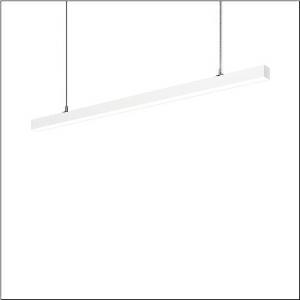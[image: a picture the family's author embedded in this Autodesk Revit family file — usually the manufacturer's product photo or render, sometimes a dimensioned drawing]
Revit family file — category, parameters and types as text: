
# Revit family: silica_r__21_51mx30db45wb_134d
name_source: partatom
category: Lighting Fixtures
units: mm (PartAtom-declared; Revit-internal decimal feet)

## family parameters
Cut with Voids When Loaded = No
Host = Face
Light Source = No
Part Type = Normal
Room Calculation Point = No
Round Connector Dimension = Use Diameter
Shared = No

## types (1)
- --- (1 x LED, 5260 lm, 32 W, 4000K)
    Apparent Load = 32 VA
    CIE Flux Codes = 47 79 96 57 100
    Color Rendering = 80
    Color Temperature = 4000K
    Default Elevation = 1800 mm
    Description = Silica® 21, office luminaire, primary optical cover: cover, of PMMA, opal, light emission: direct/indirect distribution, primary light characteristic: symmetric, installation type: suspended mounting, LED, rated luminous flux: 5.260lm, luminous efficacy: 164lm/W, light colour: 840, colour temperature: 4000K, control gear: DALI 2, with terminal, 3+2-pole, max. 2.5mm², mains connection: 220..240V, AC, 50/60Hz, rated input power: 32W, luminaire housing, of aluminium, traffic white (RAL 9016), length: 1.504mm, width: 53mm, height: 53mm, protection rating (complete): IP20, insulation class (complete): insulation class I (protective earthing), certification: CE, permissible operating ambient temperature: 0..+35°C, standard: EN 50419, packaging unit: 1 piece
    Height = 53 mm
    Lamp = 1 x LED
    Lamp Light Flux = 5260 lm
    Lamp Power = 32 W
    Lamp count = 1
    Length = 1504 mm
    Luminous efficacy = 164 lm/W
    Manufacturer = Siteco
    ModVariant = No
    Model = 51MX30DB45WB
    Mounting Place = Ceiling
    Mounting Type = Pendant
    Number of Poles = 1
    OnlyDefault = Yes
    Power Factor = 1
    Product Name = Silica® 21
    Product group = office luminaire | ceiling pendant
    ProductGroupID = 904
    Protection Class = Protection class I
    Protection Degree = IP 20
    RLX_Detail_Level = 1
    RLX_Emergency_Light_Flux = 0 lm
    RLX_Emergency_Type = 0
    RLX_Emergency_Type_DB = No
    RlxData = <blob elided: 18353 chars, md5=77b3be95>
    Socket = socket
    Standby Power = 0 W
    System Light Flux = 5260 lm
    System Power = 32 W
    Type Comments = factory setting: luminous flux: 100 % | dim-lin: 254 | 218 mA
    Type Image = l_1349027.jpg
    URL = http://relux.com
    VarID = @adj_116810
    Voltage = 0 V
    Weight = 0.00 kg
    Width = 53 mm

## geometry (parser evidence)
native form markers: Blend x4, Sweep x12
no freeform markers — native parametric forms only
